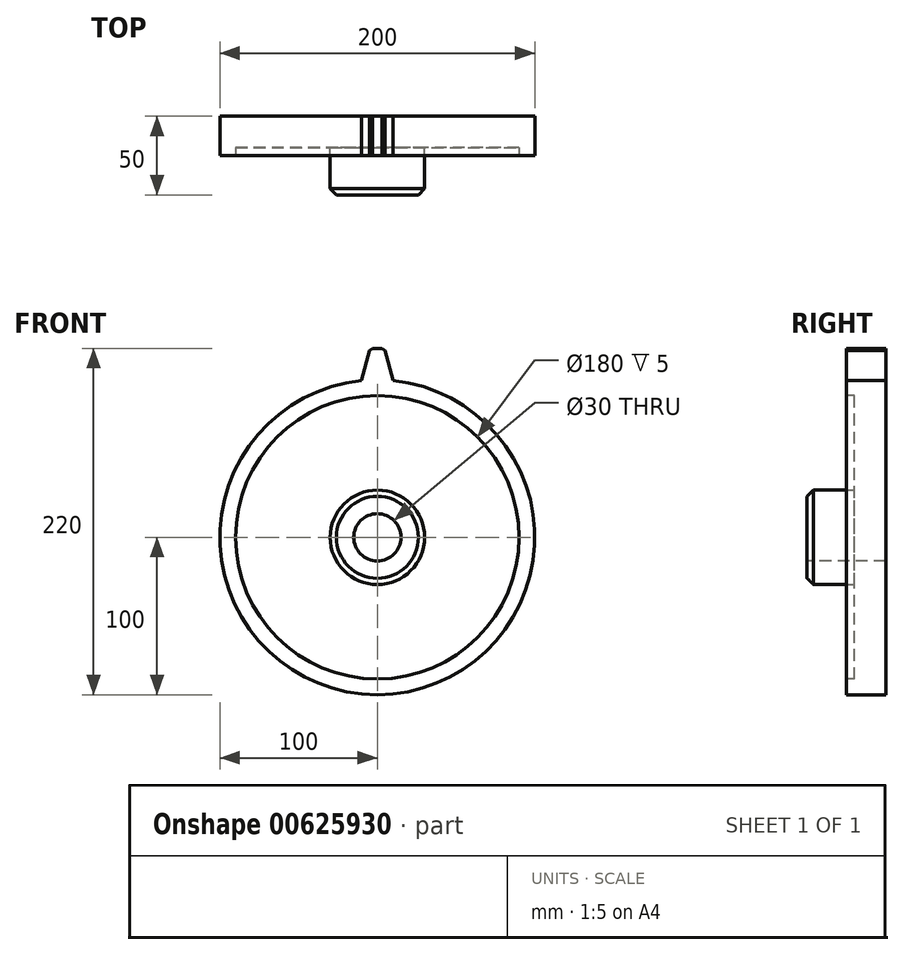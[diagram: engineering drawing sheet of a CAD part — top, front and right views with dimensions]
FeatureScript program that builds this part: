
annotation { "Feature Type Name" : "Feature", "Feature Type Description" : "" }
export const myFeature = defineFeature(function(context is Context, id is Id, definition is map)
    precondition{}
    {
        {
            var Q0;
            Q0=qCreatedBy(makeId("Front.planeOp"),FACE);
            var sketch = newSketch(context, id + "F0", { "sketchPlane" : qUnion([Q0])});
            skCircle(sketch, "E0", {"center": v(0, 0) * mm, "radius": 100 * mm});
            skSolve(sketch);
        }
        {
            var Q0;
            Q0=makeQuery(id+"F0.imprint","IMPRINT",FACE,{"disambiguationData":[TD([[makeQuery(id+"F0.imprint","IMPRINT",EDGE,{"derivedFrom":sQuery(id+"F0.wireOp",EDGE,"E0")}),1.0]])]});
            extrude(context, id + "F1", {"entities" : qUnion([Q0]), "depth" : 25 * mm, "offsetDistance" : 25 * mm});
        }
        {
            var Q0;
            Q0=qCreatedBy(makeId("Front.planeOp"),FACE);
            var sketch = newSketch(context, id + "F2", { "sketchPlane" : qUnion([Q0])});
            skLineSegment(sketch, "E1", {"start": v(-10, 99.5) * mm, "end": v(10, 99.5) * mm});
            skLineSegment(sketch, "E2", {"start": v(10, 99.5) * mm, "end": v(4.5, 120) * mm});
            skLineSegment(sketch, "E3", {"start": v(4.5, 120) * mm, "end": v(-4.5, 120) * mm});
            skLineSegment(sketch, "E4", {"start": v(-4.5, 120) * mm, "end": v(-10, 99.5) * mm});
            skSolve(sketch);
        }
        {
            var Q0;
            Q0=makeQuery(id+"F2.imprint","IMPRINT",FACE,{"disambiguationData":[TD([[makeQuery(id+"F2.imprint","IMPRINT",EDGE,{"derivedFrom":sQuery(id+"F2.wireOp",EDGE,"E1")}),1.0]])]});
            extrude(context, id + "F3", {"entities" : qUnion([Q0]), "operationType" : NewBodyOperationType.ADD, "depth" : 25 * mm, "offsetDistance" : 25 * mm});
        }
        {
            var Q0;
            Q0=makeQuery(id+"F3.opExtrude","SWEPT_EDGE",EDGE,{"disambiguationData":[OSD([sQuery(id+"F2.wireOp",EDGE,"E2"),sQuery(id+"F2.wireOp",EDGE,"E3")])]});
            var Q1;
            Q1=makeQuery(id+"F3.opExtrude","SWEPT_EDGE",EDGE,{"disambiguationData":[OSD([sQuery(id+"F2.wireOp",EDGE,"E3"),sQuery(id+"F2.wireOp",EDGE,"E4")])]});
            chamfer(context, id + "F4", {"entities" : qUnion([Q0, Q1]), "width" : 2 * mm, "tangentPropagation" : true});
        }
        {
            var Q0;
            Q0=makeQuery(id+"F3.opExtrude","SWEPT_EDGE",EDGE,{"disambiguationData":[OSD([sQuery(id+"F2.wireOp",EDGE,"E1"),sQuery(id+"F2.wireOp",EDGE,"E2")])]});
            var Q1;
            Q1=makeQuery(id+"F3.opExtrude","SWEPT_EDGE",EDGE,{"disambiguationData":[OSD([sQuery(id+"F2.wireOp",EDGE,"E1"),sQuery(id+"F2.wireOp",EDGE,"E4")])]});
            fillet(context, id + "F5", {"entities" : qUnion([Q0, Q1]), "radius" : 5 * mm, "tangentPropagation" : true, "allowEdgeOverflow" : false});
        }
        {
            var Q0;
            {var subQ0=sQuery(id+"F2.wireOp",EDGE,"E4");var subQ1=sQuery(id+"F2.wireOp",EDGE,"E3");var subQ2=sQuery(id+"F2.wireOp",EDGE,"E2");var subQ3=sQuery(id+"F2.wireOp",EDGE,"E1");Q0=makeQuery(id+"FxzjRDx70yAxBjp_1.19.F3.boolean.opBoolean","MERGE",FACE,{"derivedFrom":[makeQuery(id+"FxzjRDx70yAxBjp_1.18.F3.boolean.opBoolean","MERGE",FACE,{"derivedFrom":[makeQuery(id+"FxzjRDx70yAxBjp_1.17.F3.boolean.opBoolean","MERGE",FACE,{"derivedFrom":[makeQuery(id+"FxzjRDx70yAxBjp_1.16.F3.boolean.opBoolean","MERGE",FACE,{"derivedFrom":[makeQuery(id+"FxzjRDx70yAxBjp_1.15.F3.boolean.opBoolean","MERGE",FACE,{"derivedFrom":[makeQuery(id+"FxzjRDx70yAxBjp_1.14.F3.boolean.opBoolean","MERGE",FACE,{"derivedFrom":[makeQuery(id+"FxzjRDx70yAxBjp_1.13.F3.boolean.opBoolean","MERGE",FACE,{"derivedFrom":[makeQuery(id+"FxzjRDx70yAxBjp_1.12.F3.boolean.opBoolean","MERGE",FACE,{"derivedFrom":[makeQuery(id+"FxzjRDx70yAxBjp_1.11.F3.boolean.opBoolean","MERGE",FACE,{"derivedFrom":[makeQuery(id+"FxzjRDx70yAxBjp_1.10.F3.boolean.opBoolean","MERGE",FACE,{"derivedFrom":[makeQuery(id+"FxzjRDx70yAxBjp_1.9.F3.boolean.opBoolean","MERGE",FACE,{"derivedFrom":[makeQuery(id+"FxzjRDx70yAxBjp_1.8.F3.boolean.opBoolean","MERGE",FACE,{"derivedFrom":[makeQuery(id+"FxzjRDx70yAxBjp_1.7.F3.boolean.opBoolean","MERGE",FACE,{"derivedFrom":[makeQuery(id+"FxzjRDx70yAxBjp_1.6.F3.boolean.opBoolean","MERGE",FACE,{"derivedFrom":[makeQuery(id+"FxzjRDx70yAxBjp_1.5.F3.boolean.opBoolean","MERGE",FACE,{"derivedFrom":[makeQuery(id+"FxzjRDx70yAxBjp_1.4.F3.boolean.opBoolean","MERGE",FACE,{"derivedFrom":[makeQuery(id+"FxzjRDx70yAxBjp_1.3.F3.boolean.opBoolean","MERGE",FACE,{"derivedFrom":[makeQuery(id+"FxzjRDx70yAxBjp_1.2.F3.boolean.opBoolean","MERGE",FACE,{"derivedFrom":[makeQuery(id+"FxzjRDx70yAxBjp_1.1.F3.boolean.opBoolean","MERGE",FACE,{"derivedFrom":[makeQuery(id+"F3.boolean.opBoolean","MERGE",FACE,{"derivedFrom":[makeQuery(id+"F1.opExtrude","CAP_FACE",FACE,{"disambiguationData":[OSD([sQuery(id+"F0.wireOp",EDGE,"E0")])],"isStart":false}),makeQuery(id+"F3.opExtrude","CAP_FACE",FACE,{"disambiguationData":[OSD([subQ3,subQ2,subQ1,subQ0])],"isStart":false})]}),makeQuery(id+"FxzjRDx70yAxBjp_1.1.F3.opExtrude","CAP_FACE",FACE,{"disambiguationData":[OSD([subQ3,subQ2,subQ1,subQ0])],"isStart":false})]}),makeQuery(id+"FxzjRDx70yAxBjp_1.2.F3.opExtrude","CAP_FACE",FACE,{"disambiguationData":[OSD([subQ3,subQ2,subQ1,subQ0])],"isStart":false})]}),makeQuery(id+"FxzjRDx70yAxBjp_1.3.F3.opExtrude","CAP_FACE",FACE,{"disambiguationData":[OSD([subQ3,subQ2,subQ1,subQ0])],"isStart":false})]}),makeQuery(id+"FxzjRDx70yAxBjp_1.4.F3.opExtrude","CAP_FACE",FACE,{"disambiguationData":[OSD([subQ3,subQ2,subQ1,subQ0])],"isStart":false})]}),makeQuery(id+"FxzjRDx70yAxBjp_1.5.F3.opExtrude","CAP_FACE",FACE,{"disambiguationData":[OSD([subQ3,subQ2,subQ1,subQ0])],"isStart":false})]}),makeQuery(id+"FxzjRDx70yAxBjp_1.6.F3.opExtrude","CAP_FACE",FACE,{"disambiguationData":[OSD([subQ3,subQ2,subQ1,subQ0])],"isStart":false})]}),makeQuery(id+"FxzjRDx70yAxBjp_1.7.F3.opExtrude","CAP_FACE",FACE,{"disambiguationData":[OSD([subQ3,subQ2,subQ1,subQ0])],"isStart":false})]}),makeQuery(id+"FxzjRDx70yAxBjp_1.8.F3.opExtrude","CAP_FACE",FACE,{"disambiguationData":[OSD([subQ3,subQ2,subQ1,subQ0])],"isStart":false})]}),makeQuery(id+"FxzjRDx70yAxBjp_1.9.F3.opExtrude","CAP_FACE",FACE,{"disambiguationData":[OSD([subQ3,subQ2,subQ1,subQ0])],"isStart":false})]}),makeQuery(id+"FxzjRDx70yAxBjp_1.10.F3.opExtrude","CAP_FACE",FACE,{"disambiguationData":[OSD([subQ3,subQ2,subQ1,subQ0])],"isStart":false})]}),makeQuery(id+"FxzjRDx70yAxBjp_1.11.F3.opExtrude","CAP_FACE",FACE,{"disambiguationData":[OSD([subQ3,subQ2,subQ1,subQ0])],"isStart":false})]}),makeQuery(id+"FxzjRDx70yAxBjp_1.12.F3.opExtrude","CAP_FACE",FACE,{"disambiguationData":[OSD([subQ3,subQ2,subQ1,subQ0])],"isStart":false})]}),makeQuery(id+"FxzjRDx70yAxBjp_1.13.F3.opExtrude","CAP_FACE",FACE,{"disambiguationData":[OSD([subQ3,subQ2,subQ1,subQ0])],"isStart":false})]}),makeQuery(id+"FxzjRDx70yAxBjp_1.14.F3.opExtrude","CAP_FACE",FACE,{"disambiguationData":[OSD([subQ3,subQ2,subQ1,subQ0])],"isStart":false})]}),makeQuery(id+"FxzjRDx70yAxBjp_1.15.F3.opExtrude","CAP_FACE",FACE,{"disambiguationData":[OSD([subQ3,subQ2,subQ1,subQ0])],"isStart":false})]}),makeQuery(id+"FxzjRDx70yAxBjp_1.16.F3.opExtrude","CAP_FACE",FACE,{"disambiguationData":[OSD([subQ3,subQ2,subQ1,subQ0])],"isStart":false})]}),makeQuery(id+"FxzjRDx70yAxBjp_1.17.F3.opExtrude","CAP_FACE",FACE,{"disambiguationData":[OSD([subQ3,subQ2,subQ1,subQ0])],"isStart":false})]}),makeQuery(id+"FxzjRDx70yAxBjp_1.18.F3.opExtrude","CAP_FACE",FACE,{"disambiguationData":[OSD([subQ3,subQ2,subQ1,subQ0])],"isStart":false})]}),makeQuery(id+"FxzjRDx70yAxBjp_1.19.F3.opExtrude","CAP_FACE",FACE,{"disambiguationData":[OSD([subQ3,subQ2,subQ1,subQ0])],"isStart":false})]});}
            var sketch = newSketch(context, id + "F6", { "sketchPlane" : qUnion([Q0])});
            skCircle(sketch, "E5", {"center": v(0, 0) * mm, "radius": 90 * mm});
            skSolve(sketch);
        }
        {
            var Q0;
            Q0 = qSketchRegion(id + "F6", true);
            extrude(context, id + "F7", {"entities" : qUnion([Q0]), "operationType" : NewBodyOperationType.REMOVE, "oppositeDirection" : true, "depth" : 5 * mm, "offsetDistance" : 25 * mm});
        }
        {
            var Q0;
            Q0=makeQuery(id+"F7.boolean.opBoolean","COPY",FACE,{"derivedFrom":makeQuery(id+"F7.opExtrude","CAP_FACE",FACE,{"disambiguationData":[OSD([sQuery(id+"F6.wireOp",EDGE,"E5")])],"isStart":false})});
            var sketch = newSketch(context, id + "F8", { "sketchPlane" : qUnion([Q0])});
            skCircle(sketch, "E6", {"center": v(0, 0) * mm, "radius": 30 * mm});
            skSolve(sketch);
        }
        {
            var Q0;
            Q0 = qSketchRegion(id + "F8", true);
            extrude(context, id + "F9", {"entities" : qUnion([Q0]), "operationType" : NewBodyOperationType.ADD, "depth" : 30 * mm, "offsetDistance" : 25 * mm});
        }
        {
            var Q0;
            Q0=makeQuery(id+"F9.opExtrude","CAP_FACE",FACE,{"disambiguationData":[OSD([sQuery(id+"F8.wireOp",EDGE,"E6")])],"isStart":false});
            var sketch = newSketch(context, id + "F10", { "sketchPlane" : qUnion([Q0])});
            skCircle(sketch, "E7", {"center": v(0, 0) * mm, "radius": 15 * mm});
            skSolve(sketch);
        }
        {
            var Q0;
            Q0=makeQuery(id+"F10.imprint","IMPRINT",FACE,{"disambiguationData":[TD([[makeQuery(id+"F10.imprint","IMPRINT",EDGE,{"derivedFrom":sQuery(id+"F10.wireOp",EDGE,"E7")}),1.0]])]});
            extrude(context, id + "F11", {"entities" : qUnion([Q0]), "operationType" : NewBodyOperationType.REMOVE, "endBound" : BoundingType.THROUGH_ALL, "oppositeDirection" : true, "depth" : 25 * mm, "offsetDistance" : 25 * mm});
        }
        {
            var Q0;
            Q0=makeQuery(id+"F9.opExtrude","CAP_EDGE",EDGE,{"disambiguationData":[OSD([sQuery(id+"F8.wireOp",EDGE,"E6")])],"isStart":false});
            var Q1;
            Q1=makeQuery(id+"F11.boolean.opBoolean","COPY",EDGE,{"derivedFrom":makeQuery(id+"F11.opExtrude","CAP_EDGE",EDGE,{"disambiguationData":[OSD([sQuery(id+"F10.wireOp",EDGE,"E7")])],"isStart":true})});
            chamfer(context, id + "F12", {"entities" : qUnion([Q0, Q1]), "width" : 4 * mm, "tangentPropagation" : true});
        }
    });
